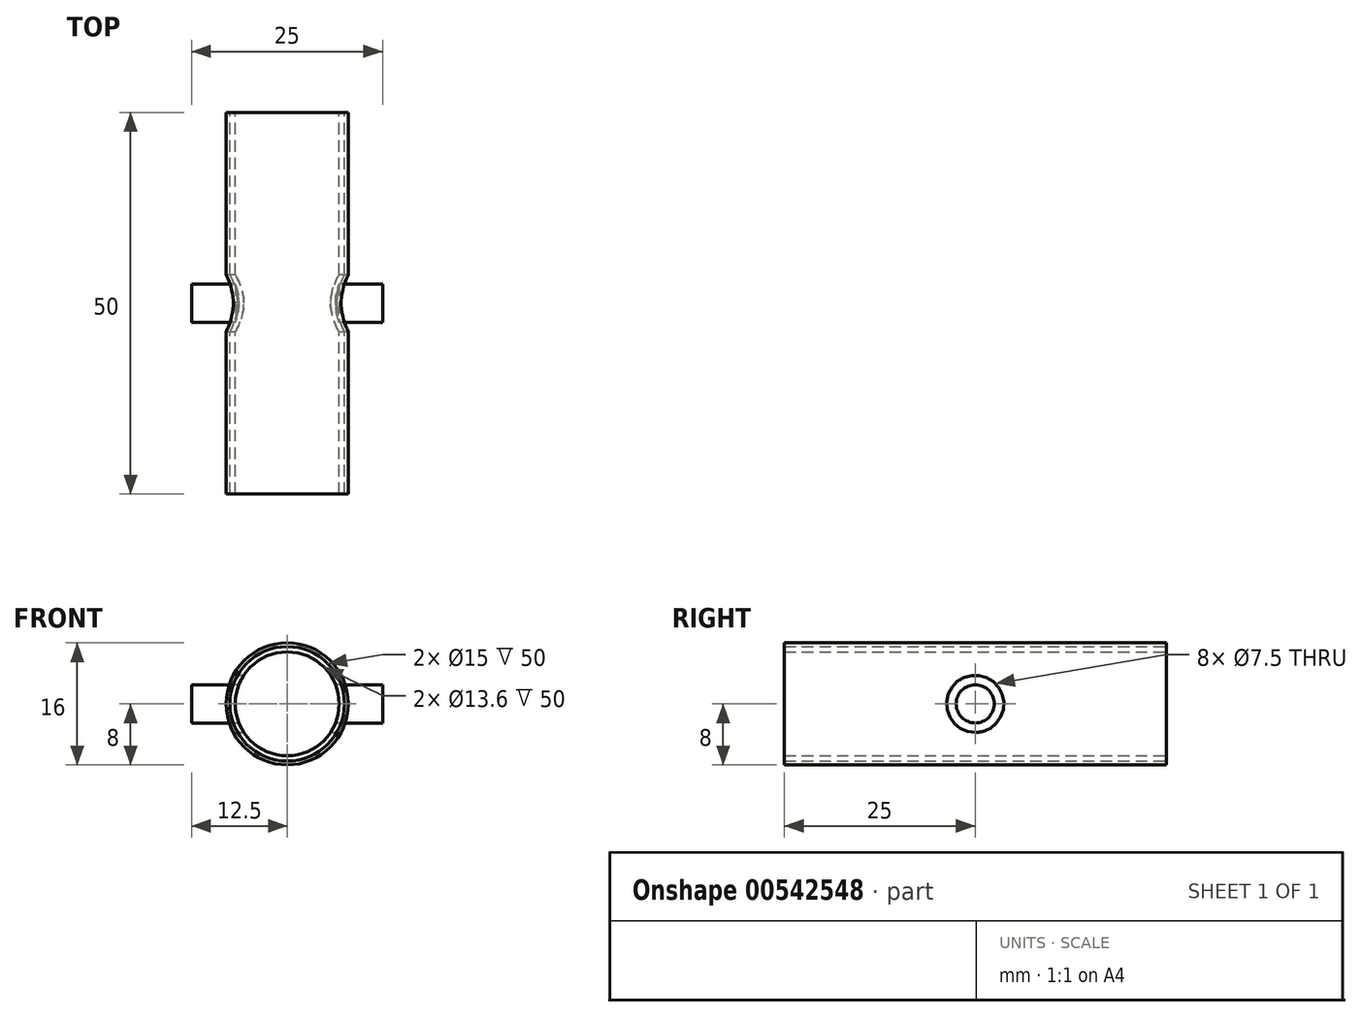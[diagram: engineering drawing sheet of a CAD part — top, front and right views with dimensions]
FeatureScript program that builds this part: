
annotation { "Feature Type Name" : "Feature", "Feature Type Description" : "" }
export const myFeature = defineFeature(function(context is Context, id is Id, definition is map)
    precondition{}
    {
        {
            var Q0;
            Q0=qCreatedBy(makeId("Front.planeOp"),FACE);
            var sketch = newSketch(context, id + "F0", { "sketchPlane" : qUnion([Q0])});
            skCircle(sketch, "E0", {"center": v(0, 0) * mm, "radius": 6.8 * mm});
            skCircle(sketch, "E1", {"center": v(0, 0) * mm, "radius": 7.5 * mm});
            skCircle(sketch, "E2", {"center": v(0, 0) * mm, "radius": 8 * mm});
            skSolve(sketch);
        }
        {
            var Q0;
            Q0=makeQuery(id+"F0.imprint","IMPRINT",FACE,{"disambiguationData":[TD([[makeQuery(id+"F0.imprint","IMPRINT",EDGE,{"derivedFrom":sQuery(id+"F0.wireOp",EDGE,"E0")}),-1.0]])]});
            extrude(context, id + "F1", {"entities" : qUnion([Q0]), "endBound" : BoundingType.SYMMETRIC, "depth" : 50 * mm, "offsetDistance" : 25 * mm});
        }
        {
            var Q0;
            Q0=makeQuery(id+"F0.imprint","IMPRINT",FACE,{"disambiguationData":[TD([[makeQuery(id+"F0.imprint","IMPRINT",EDGE,{"derivedFrom":sQuery(id+"F0.wireOp",EDGE,"E1")}),-1.0]])]});
            extrude(context, id + "F2", {"entities" : qUnion([Q0]), "endBound" : BoundingType.SYMMETRIC, "depth" : 50 * mm, "offsetDistance" : 25 * mm});
        }
        {
            var Q0;
            Q0=qCreatedBy(makeId("Right.planeOp"),FACE);
            var sketch = newSketch(context, id + "F3", { "sketchPlane" : qUnion([Q0])});
            skCircle(sketch, "E3", {"center": v(0, 0) * mm, "radius": 2.5 * mm});
            skSolve(sketch);
        }
        {
            var Q0;
            Q0 = qSketchRegion(id + "F3", true);
            extrude(context, id + "F4", {"entities" : qUnion([Q0]), "operationType" : NewBodyOperationType.REMOVE, "endBound" : BoundingType.THROUGH_ALL, "oppositeDirection" : true, "depth" : 25 * mm, "offsetDistance" : 25 * mm, "hasSecondDirection" : true, "secondDirectionBound" : SecondDirectionBoundingType.THROUGH_ALL, "secondDirectionOppositeDirection" : false, "secondDirectionDepth" : 25 * mm});
        }
        {
            var Q0;
            Q0=qCreatedBy(makeId("Right.planeOp"),FACE);
            var sketch = newSketch(context, id + "F5", { "sketchPlane" : qUnion([Q0])});
            skCircle(sketch, "E4", {"center": v(0, 0) * mm, "radius": 3.75 * mm});
            skSolve(sketch);
        }
        {
            var Q0;
            Q0 = qSketchRegion(id + "F5", true);
            extrude(context, id + "F6", {"entities" : qUnion([Q0]), "operationType" : NewBodyOperationType.REMOVE, "endBound" : BoundingType.THROUGH_ALL, "oppositeDirection" : true, "depth" : 25 * mm, "offsetDistance" : 25 * mm, "hasSecondDirection" : true, "secondDirectionBound" : SecondDirectionBoundingType.THROUGH_ALL, "secondDirectionOppositeDirection" : false, "secondDirectionDepth" : 25 * mm});
        }
        {
            var Q0;
            Q0 = qSketchRegion(id + "F3", true);
            extrude(context, id + "F7", {"entities" : qUnion([Q0]), "endBound" : BoundingType.SYMMETRIC, "depth" : 25 * mm, "offsetDistance" : 25 * mm});
        }
        {
            var Q0;
            Q0=makeQuery(id+"F0.imprint","IMPRINT",FACE,{"disambiguationData":[TD([[makeQuery(id+"F0.imprint","IMPRINT",EDGE,{"derivedFrom":sQuery(id+"F0.wireOp",EDGE,"E0")}),1.0]])]});
            extrude(context, id + "F8", {"entities" : qUnion([Q0]), "operationType" : NewBodyOperationType.REMOVE, "endBound" : BoundingType.THROUGH_ALL, "oppositeDirection" : true, "depth" : 25 * mm, "offsetDistance" : 25 * mm, "hasSecondDirection" : true, "secondDirectionBound" : SecondDirectionBoundingType.THROUGH_ALL, "secondDirectionOppositeDirection" : false, "secondDirectionDepth" : 25 * mm});
        }
    });
